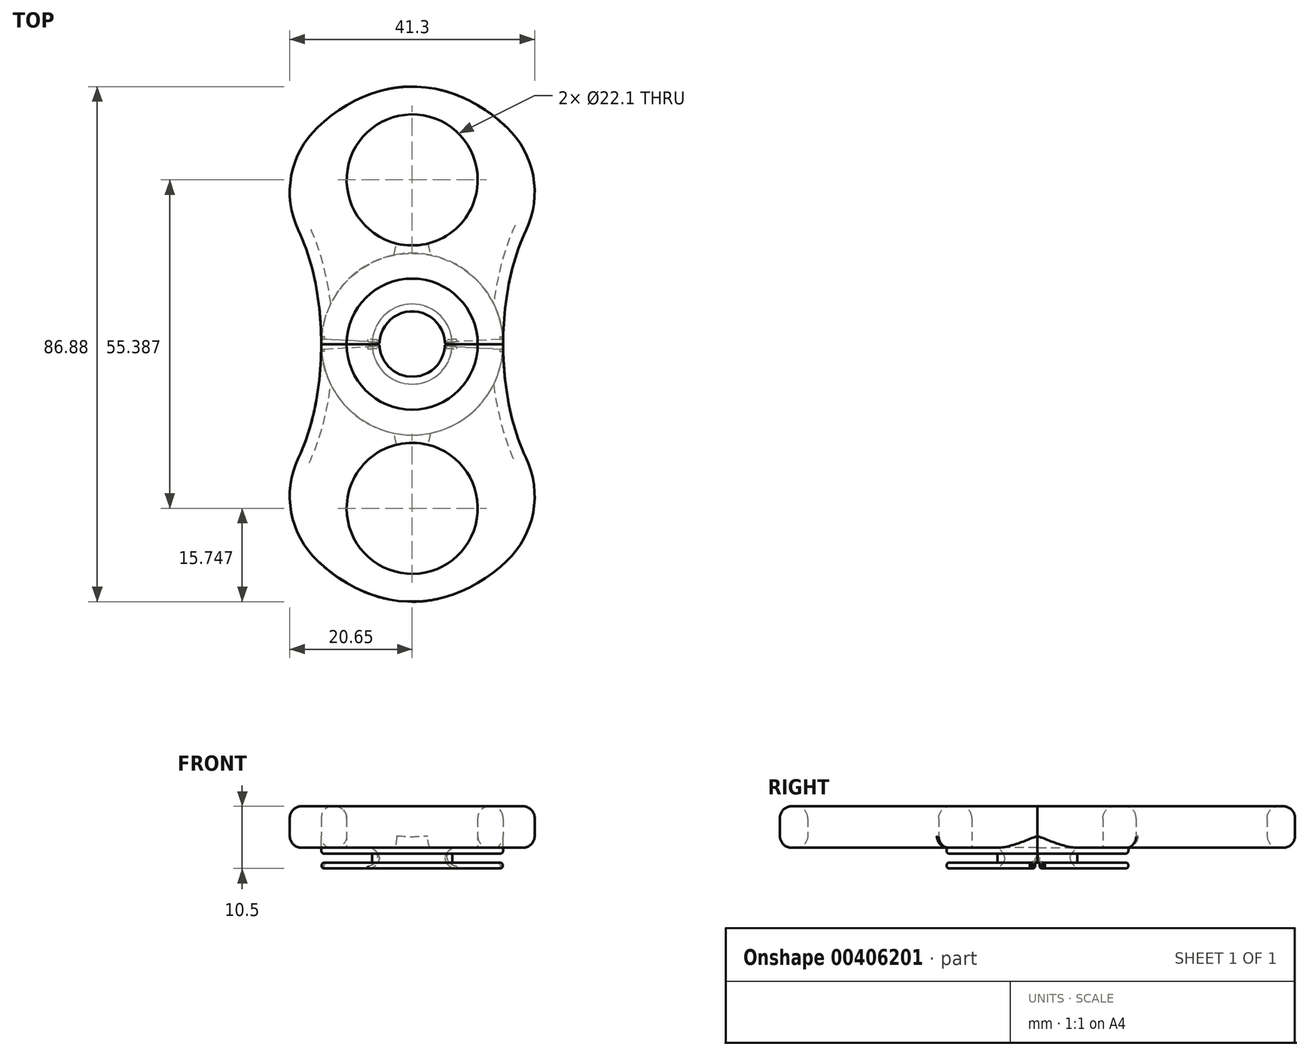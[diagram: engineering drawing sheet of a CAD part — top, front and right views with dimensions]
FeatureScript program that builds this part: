
annotation { "Feature Type Name" : "Feature", "Feature Type Description" : "" }
export const myFeature = defineFeature(function(context is Context, id is Id, definition is map)
    precondition{}
    {
        {
            var Q0;
            Q0=qCreatedBy(makeId("Top.planeOp"),FACE);
            var sketch = newSketch(context, id + "F0", { "sketchPlane" : qUnion([Q0])});
            skCircle(sketch, "E0", {"center": v(0, 0) * mm, "radius": 11.05 * mm});
            skEllipse(sketch, "E1", {"center": v(0, 0) * mm, "majorRadius": 43.44 * mm, "minorRadius": 29.52 * mm, "majorAxis": v(0, 1)});
            skEllipse(sketch, "E2", {"center": v(29.52, 0) * mm, "majorRadius": 28 * mm, "minorRadius": 14.19 * mm, "majorAxis": v(0, -1)});
            skLineSegment(sketch, "E3", {"start": v(0, 58.33) * mm, "end": v(0, -59.11) * mm});
            skEllipse(sketch, "E4", {"center": v(-29.52, 0) * mm, "majorRadius": 27.94 * mm, "minorRadius": 14.94 * mm, "majorAxis": v(0, 1)});
            skCircle(sketch, "E5", {"center": v(0, 27.7) * mm, "radius": 11.05 * mm});
            skLineSegment(sketch, "E6", {"start": v(54.05, 0) * mm, "end": v(-64.12, 0) * mm});
            skCircle(sketch, "E7", {"center": v(0, 0) * mm, "radius": 5.5 * mm});
            skCircle(sketch, "E8", {"center": v(0, 0) * mm, "radius": 15.34 * mm});
            skCircle(sketch, "E9", {"center": v(0, 0) * mm, "radius": 6.75 * mm});
            skSolve(sketch);
        }
        {
            var Q0;
            {var subQ1=sQuery(id+"F0.wireOp",EDGE,"E3");var subQ5=sQuery(id+"F0.wireOp",EDGE,"E0");var subQ6=makeQuery(id+"F0.imprint","INTERSECT",VERTEX,{"disambiguationData":[OD(0.0)],"derivedFrom":[subQ5,subQ1]});Q0=makeQuery(id+"F0.imprint","IMPRINT",FACE,{"disambiguationData":[TD([[makeQuery(id+"F0.imprint","IMPRINT",EDGE,{"disambiguationData":[TD([[subQ6,1.0]])],"derivedFrom":subQ5}),-1.0]])]});}
            var Q1;
            {var subQ1=sQuery(id+"F0.wireOp",EDGE,"E3");var subQ6=sQuery(id+"F0.wireOp",EDGE,"E1");var subQ9=makeQuery(id+"F0.imprint","INTERSECT",VERTEX,{"disambiguationData":[OD(0.0)],"derivedFrom":[subQ6,subQ1]});Q1=makeQuery(id+"F0.imprint","IMPRINT",FACE,{"disambiguationData":[TD([[makeQuery(id+"F0.imprint","IMPRINT",EDGE,{"disambiguationData":[TD([[subQ9,1.0]])],"derivedFrom":subQ6}),1.0]])]});}
            extrude(context, id + "F1", {"entities" : qUnion([Q0, Q1]), "depth" : 7 * mm});
        }
        {
            var Q0;
            {var subQ0=sQuery(id+"F0.wireOp",EDGE,"E3");var subQ1=sQuery(id+"F0.wireOp",EDGE,"E0");var subQ2=makeQuery(id+"F0.imprint","INTERSECT",VERTEX,{"disambiguationData":[OD(0.0)],"derivedFrom":[subQ1,subQ0]});Q0=makeQuery(id+"F0.imprint","IMPRINT",FACE,{"disambiguationData":[TD([[makeQuery(id+"F0.imprint","IMPRINT",EDGE,{"disambiguationData":[TD([[subQ2,1.0]])],"derivedFrom":subQ1}),-1.0]])]});}
            var Q1;
            {var subQ0=sQuery(id+"F0.wireOp",EDGE,"E3");var subQ1=sQuery(id+"F0.wireOp",EDGE,"E0");var subQ2=makeQuery(id+"F0.imprint","INTERSECT",VERTEX,{"disambiguationData":[OD(0.0)],"derivedFrom":[subQ1,subQ0]});Q1=makeQuery(id+"F0.imprint","IMPRINT",FACE,{"disambiguationData":[TD([[makeQuery(id+"F0.imprint","IMPRINT",EDGE,{"disambiguationData":[TD([[subQ2,1.0]])],"derivedFrom":subQ1}),1.0]])]});}
            var Q2;
            {var subQ0=sQuery(id+"F0.wireOp",EDGE,"E9");var subQ1=sQuery(id+"F0.wireOp",EDGE,"E3");var subQ2=makeQuery(id+"F0.imprint","INTERSECT",VERTEX,{"disambiguationData":[OD(0.0)],"derivedFrom":[subQ1,subQ0]});Q2=makeQuery(id+"F0.imprint","IMPRINT",FACE,{"disambiguationData":[TD([[makeQuery(id+"F0.imprint","IMPRINT",EDGE,{"disambiguationData":[TD([[subQ2,-1.0]])],"derivedFrom":subQ1}),1.0]])]});}
            extrude(context, id + "F2", {"entities" : qUnion([Q0, Q1, Q2]), "operationType" : NewBodyOperationType.ADD, "oppositeDirection" : true, "depth" : 1 * mm});
        }
        {
            var Q0;
            {var subQ0=sQuery(id+"F0.wireOp",EDGE,"E9");var subQ1=sQuery(id+"F0.wireOp",EDGE,"E3");var subQ2=makeQuery(id+"F0.imprint","INTERSECT",VERTEX,{"disambiguationData":[OD(0.0)],"derivedFrom":[subQ1,subQ0]});Q0=makeQuery(id+"F0.imprint","IMPRINT",FACE,{"disambiguationData":[TD([[makeQuery(id+"F0.imprint","IMPRINT",EDGE,{"disambiguationData":[TD([[subQ2,-1.0]])],"derivedFrom":subQ1}),1.0]])]});}
            extrude(context, id + "F3", {"entities" : qUnion([Q0]), "operationType" : NewBodyOperationType.ADD, "oppositeDirection" : true, "depth" : 2.5 * mm});
        }
        {
            var Q0;
            {var subQ0=sQuery(id+"F0.wireOp",EDGE,"E9");var subQ1=sQuery(id+"F0.wireOp",EDGE,"E3");var subQ2=makeQuery(id+"F0.imprint","INTERSECT",VERTEX,{"disambiguationData":[OD(0.0)],"derivedFrom":[subQ1,subQ0]});Q0=makeQuery(id+"F0.imprint","IMPRINT",FACE,{"disambiguationData":[TD([[makeQuery(id+"F0.imprint","IMPRINT",EDGE,{"disambiguationData":[TD([[subQ2,-1.0]])],"derivedFrom":subQ1}),1.0]])]});}
            var Q1;
            {var subQ0=sQuery(id+"F0.wireOp",EDGE,"E3");var subQ1=sQuery(id+"F0.wireOp",EDGE,"E0");var subQ2=makeQuery(id+"F0.imprint","INTERSECT",VERTEX,{"disambiguationData":[OD(0.0)],"derivedFrom":[subQ1,subQ0]});Q1=makeQuery(id+"F0.imprint","IMPRINT",FACE,{"disambiguationData":[TD([[makeQuery(id+"F0.imprint","IMPRINT",EDGE,{"disambiguationData":[TD([[subQ2,1.0]])],"derivedFrom":subQ1}),1.0]])]});}
            var Q2;
            {var subQ0=sQuery(id+"F0.wireOp",EDGE,"E3");var subQ1=sQuery(id+"F0.wireOp",EDGE,"E0");var subQ2=makeQuery(id+"F0.imprint","INTERSECT",VERTEX,{"disambiguationData":[OD(0.0)],"derivedFrom":[subQ1,subQ0]});Q2=makeQuery(id+"F0.imprint","IMPRINT",FACE,{"disambiguationData":[TD([[makeQuery(id+"F0.imprint","IMPRINT",EDGE,{"disambiguationData":[TD([[subQ2,1.0]])],"derivedFrom":subQ1}),-1.0]])]});}
            extrude(context, id + "F4", {"entities" : qUnion([Q0, Q1, Q2]), "operationType" : NewBodyOperationType.ADD, "oppositeDirection" : true, "depth" : 3.5 * mm, "hasSecondDirection" : true, "secondDirectionOppositeDirection" : true, "secondDirectionDepth" : 2.5 * mm});
        }
        {
            var Q0;
            Q0=makeQuery(id+"F1.opExtrude","SWEPT_BODY",BODY,{"disambiguationData":[OSD([sQuery(id+"F0.wireOp",EDGE,"E0"),sQuery(id+"F0.wireOp",EDGE,"E1"),sQuery(id+"F0.wireOp",EDGE,"E2"),sQuery(id+"F0.wireOp",EDGE,"E3"),sQuery(id+"F0.wireOp",EDGE,"E5"),sQuery(id+"F0.wireOp",EDGE,"E6")])]});
            var Q1;
            Q1=qCreatedBy(makeId("Right.planeOp"),FACE);
            mirror(context, id + "F5", {"operationType" : NewBodyOperationType.ADD, "entities" : qUnion([Q0]), "mirrorPlane" : qUnion([Q1])});
        }
        {
            var Q0;
            {var subQ0=sQuery(id+"F0.wireOp",EDGE,"E6");var subQ1=sQuery(id+"F0.wireOp",EDGE,"E3");var subQ2=makeQuery(id+"F0.imprint","INTERSECT",VERTEX,{"derivedFrom":[subQ1,subQ0]});Q0=makeQuery(id+"F0.imprint","IMPRINT",FACE,{"disambiguationData":[TD([[makeQuery(id+"F0.imprint","IMPRINT",EDGE,{"disambiguationData":[TD([[subQ2,-1.0]])],"derivedFrom":subQ1}),-1.0]])]});}
            var Q1;
            {var subQ0=sQuery(id+"F0.wireOp",EDGE,"E7");var subQ1=sQuery(id+"F0.wireOp",EDGE,"E3");var subQ2=makeQuery(id+"F0.imprint","INTERSECT",VERTEX,{"disambiguationData":[OD(0.0)],"derivedFrom":[subQ1,subQ0]});Q1=makeQuery(id+"F0.imprint","IMPRINT",FACE,{"disambiguationData":[TD([[makeQuery(id+"F0.imprint","IMPRINT",EDGE,{"disambiguationData":[TD([[subQ2,-1.0]])],"derivedFrom":subQ1}),-1.0]])]});}
            var Q2;
            {var subQ0=sQuery(id+"F0.wireOp",EDGE,"E7");var subQ1=sQuery(id+"F0.wireOp",EDGE,"E3");var subQ2=makeQuery(id+"F0.imprint","INTERSECT",VERTEX,{"disambiguationData":[OD(0.0)],"derivedFrom":[subQ1,subQ0]});Q2=makeQuery(id+"F0.imprint","IMPRINT",FACE,{"disambiguationData":[TD([[makeQuery(id+"F0.imprint","IMPRINT",EDGE,{"disambiguationData":[TD([[subQ2,-1.0]])],"derivedFrom":subQ1}),1.0]])]});}
            var Q3;
            {var subQ0=sQuery(id+"F0.wireOp",EDGE,"E6");var subQ1=sQuery(id+"F0.wireOp",EDGE,"E3");var subQ2=makeQuery(id+"F0.imprint","INTERSECT",VERTEX,{"derivedFrom":[subQ1,subQ0]});Q3=makeQuery(id+"F0.imprint","IMPRINT",FACE,{"disambiguationData":[TD([[makeQuery(id+"F0.imprint","IMPRINT",EDGE,{"disambiguationData":[TD([[subQ2,-1.0]])],"derivedFrom":subQ1}),1.0]])]});}
            extrude(context, id + "F6", {"entities" : qUnion([Q0, Q1, Q2, Q3]), "depth" : 22.66 * mm, "hasSecondDirection" : true, "secondDirectionOppositeDirection" : false, "secondDirectionDepth" : 15.2 * mm});
        }
        {
            var Q0;
            {var subQ0=makeQuery(id+"F4.opExtrude","CAP_FACE",FACE,{"disambiguationData":[OSD([sQuery(id+"F0.wireOp",EDGE,"E3"),sQuery(id+"F0.wireOp",EDGE,"E6"),sQuery(id+"F0.wireOp",EDGE,"E7"),sQuery(id+"F0.wireOp",EDGE,"E8")])],"isStart":false});Q0=makeQuery(id+"F5.boolean.opBoolean","MERGE",FACE,{"derivedFrom":[subQ0,makeQuery(id+"F5.opPattern","COPY",FACE,{"derivedFrom":subQ0,"instanceName":"1"})]});}
            var sketch = newSketch(context, id + "F7", { "sketchPlane" : qUnion([Q0])});
            skLineSegment(sketch, "E10", {"start": v(0, -18) * mm, "end": v(-1, -18) * mm});
            skLineSegment(sketch, "E11", {"start": v(-1, -18) * mm, "end": v(0, 0) * mm});
            skLineSegment(sketch, "E12", {"start": v(0, 0) * mm, "end": v(1, -18) * mm});
            skLineSegment(sketch, "E13", {"start": v(1, -18) * mm, "end": v(0, -18) * mm});
            skLineSegment(sketch, "E14.1.0", {"start": v(8.13, -16.09) * mm, "end": v(0, 0) * mm});
            skLineSegment(sketch, "E14.1.1", {"start": v(0, 0) * mm, "end": v(9.87, -15.09) * mm});
            skLineSegment(sketch, "E14.1.2", {"start": v(9, -15.59) * mm, "end": v(8.13, -16.09) * mm});
            skLineSegment(sketch, "E14.1.3", {"start": v(9.87, -15.09) * mm, "end": v(9, -15.59) * mm});
            skLineSegment(sketch, "E14.2.0", {"start": v(15.09, -9.87) * mm, "end": v(0, 0) * mm});
            skLineSegment(sketch, "E14.2.1", {"start": v(0, 0) * mm, "end": v(16.09, -8.13) * mm});
            skLineSegment(sketch, "E14.2.2", {"start": v(15.59, -9) * mm, "end": v(15.09, -9.87) * mm});
            skLineSegment(sketch, "E14.2.3", {"start": v(16.09, -8.13) * mm, "end": v(15.59, -9) * mm});
            skLineSegment(sketch, "E14.3.0", {"start": v(18, -1) * mm, "end": v(0, 0) * mm});
            skLineSegment(sketch, "E14.3.1", {"start": v(0, 0) * mm, "end": v(18, 1) * mm});
            skLineSegment(sketch, "E14.3.2", {"start": v(18, 0) * mm, "end": v(18, -1) * mm});
            skLineSegment(sketch, "E14.3.3", {"start": v(18, 1) * mm, "end": v(18, 0) * mm});
            skLineSegment(sketch, "E14.4.0", {"start": v(16.09, 8.13) * mm, "end": v(0, 0) * mm});
            skLineSegment(sketch, "E14.4.1", {"start": v(0, 0) * mm, "end": v(15.09, 9.87) * mm});
            skLineSegment(sketch, "E14.4.2", {"start": v(15.59, 9) * mm, "end": v(16.09, 8.13) * mm});
            skLineSegment(sketch, "E14.4.3", {"start": v(15.09, 9.87) * mm, "end": v(15.59, 9) * mm});
            skLineSegment(sketch, "E14.5.0", {"start": v(9.87, 15.09) * mm, "end": v(0, 0) * mm});
            skLineSegment(sketch, "E14.5.1", {"start": v(0, 0) * mm, "end": v(8.13, 16.09) * mm});
            skLineSegment(sketch, "E14.5.2", {"start": v(9, 15.59) * mm, "end": v(9.87, 15.09) * mm});
            skLineSegment(sketch, "E14.5.3", {"start": v(8.13, 16.09) * mm, "end": v(9, 15.59) * mm});
            skLineSegment(sketch, "E14.6.0", {"start": v(1, 18) * mm, "end": v(0, 0) * mm});
            skLineSegment(sketch, "E14.6.1", {"start": v(0, 0) * mm, "end": v(-1, 18) * mm});
            skLineSegment(sketch, "E14.6.2", {"start": v(0, 18) * mm, "end": v(1, 18) * mm});
            skLineSegment(sketch, "E14.6.3", {"start": v(-1, 18) * mm, "end": v(0, 18) * mm});
            skLineSegment(sketch, "E14.7.0", {"start": v(-8.13, 16.09) * mm, "end": v(0, 0) * mm});
            skLineSegment(sketch, "E14.7.1", {"start": v(0, 0) * mm, "end": v(-9.87, 15.09) * mm});
            skLineSegment(sketch, "E14.7.2", {"start": v(-9, 15.59) * mm, "end": v(-8.13, 16.09) * mm});
            skLineSegment(sketch, "E14.7.3", {"start": v(-9.87, 15.09) * mm, "end": v(-9, 15.59) * mm});
            skLineSegment(sketch, "E14.8.0", {"start": v(-15.09, 9.87) * mm, "end": v(0, 0) * mm});
            skLineSegment(sketch, "E14.8.1", {"start": v(0, 0) * mm, "end": v(-16.09, 8.13) * mm});
            skLineSegment(sketch, "E14.8.2", {"start": v(-15.59, 9) * mm, "end": v(-15.09, 9.87) * mm});
            skLineSegment(sketch, "E14.8.3", {"start": v(-16.09, 8.13) * mm, "end": v(-15.59, 9) * mm});
            skLineSegment(sketch, "E14.9.0", {"start": v(-18, 1) * mm, "end": v(0, 0) * mm});
            skLineSegment(sketch, "E14.9.1", {"start": v(0, 0) * mm, "end": v(-18, -1) * mm});
            skLineSegment(sketch, "E14.9.2", {"start": v(-18, 0) * mm, "end": v(-18, 1) * mm});
            skLineSegment(sketch, "E14.9.3", {"start": v(-18, -1) * mm, "end": v(-18, 0) * mm});
            skLineSegment(sketch, "E14.10.0", {"start": v(-16.09, -8.13) * mm, "end": v(0, 0) * mm});
            skLineSegment(sketch, "E14.10.1", {"start": v(0, 0) * mm, "end": v(-15.09, -9.87) * mm});
            skLineSegment(sketch, "E14.10.2", {"start": v(-15.59, -9) * mm, "end": v(-16.09, -8.13) * mm});
            skLineSegment(sketch, "E14.10.3", {"start": v(-15.09, -9.87) * mm, "end": v(-15.59, -9) * mm});
            skLineSegment(sketch, "E14.11.0", {"start": v(-9.87, -15.09) * mm, "end": v(0, 0) * mm});
            skLineSegment(sketch, "E14.11.1", {"start": v(0, 0) * mm, "end": v(-8.13, -16.09) * mm});
            skLineSegment(sketch, "E14.11.2", {"start": v(-9, -15.59) * mm, "end": v(-9.87, -15.09) * mm});
            skLineSegment(sketch, "E14.11.3", {"start": v(-8.13, -16.09) * mm, "end": v(-9, -15.59) * mm});
            skPoint(sketch, "E14.center", {"position": v(0, 0) * mm});
            skSolve(sketch);
        }
        {
            var Q0;
            {var subQ0=makeQuery(id+"F1.opExtrude","CAP_EDGE",EDGE,{"disambiguationData":[OSD([sQuery(id+"F0.wireOp",EDGE,"E5")])],"isStart":true});Q0=makeQuery(id+"F5.boolean.opBoolean","MERGE",EDGE,{"derivedFrom":[subQ0,makeQuery(id+"F5.opPattern","COPY",EDGE,{"derivedFrom":subQ0,"instanceName":"1"})]});}
            var Q1;
            Q1=makeQuery(id+"F1.opExtrude","CAP_EDGE",EDGE,{"disambiguationData":[OSD([sQuery(id+"F0.wireOp",EDGE,"E2")])],"isStart":true});
            var Q2;
            Q2=makeQuery(id+"F1.opExtrude","CAP_EDGE",EDGE,{"disambiguationData":[OSD([sQuery(id+"F0.wireOp",EDGE,"E2")])],"isStart":false});
            var Q3;
            Q3=makeQuery(id+"F5.opPattern","COPY",EDGE,{"derivedFrom":makeQuery(id+"F1.opExtrude","CAP_EDGE",EDGE,{"disambiguationData":[OSD([sQuery(id+"F0.wireOp",EDGE,"E2")])],"isStart":true}),"instanceName":"1"});
            var Q4;
            {var subQ0=makeQuery(id+"F1.opExtrude","CAP_EDGE",EDGE,{"disambiguationData":[OSD([sQuery(id+"F0.wireOp",EDGE,"E1")])],"isStart":true});Q4=makeQuery(id+"F5.boolean.opBoolean","MERGE",EDGE,{"derivedFrom":[subQ0,makeQuery(id+"F5.opPattern","COPY",EDGE,{"derivedFrom":subQ0,"instanceName":"1"})]});}
            var Q5;
            {var subQ0=makeQuery(id+"F4.opExtrude","CAP_EDGE",EDGE,{"disambiguationData":[OSD([sQuery(id+"F0.wireOp",EDGE,"E7")])],"isStart":false});Q5=makeQuery(id+"F5.boolean.opBoolean","MERGE",EDGE,{"derivedFrom":[subQ0,makeQuery(id+"F5.opPattern","COPY",EDGE,{"derivedFrom":subQ0,"instanceName":"1"})]});}
            var Q6;
            {var subQ0=makeQuery(id+"F2.opExtrude","CAP_EDGE",EDGE,{"disambiguationData":[OSD([sQuery(id+"F0.wireOp",EDGE,"E7")])],"isStart":true});Q6=makeQuery(id+"F5.boolean.opBoolean","MERGE",EDGE,{"derivedFrom":[subQ0,makeQuery(id+"F5.opPattern","COPY",EDGE,{"derivedFrom":subQ0,"instanceName":"1"})]});}
            var Q7;
            {var subQ0=makeQuery(id+"F1.opExtrude","CAP_EDGE",EDGE,{"disambiguationData":[OSD([sQuery(id+"F0.wireOp",EDGE,"E1")])],"isStart":false});Q7=makeQuery(id+"F5.boolean.opBoolean","MERGE",EDGE,{"derivedFrom":[subQ0,makeQuery(id+"F5.opPattern","COPY",EDGE,{"derivedFrom":subQ0,"instanceName":"1"})]});}
            var Q8;
            {var subQ0=makeQuery(id+"F1.opExtrude","CAP_EDGE",EDGE,{"disambiguationData":[OSD([sQuery(id+"F0.wireOp",EDGE,"E5")])],"isStart":false});Q8=makeQuery(id+"F5.boolean.opBoolean","MERGE",EDGE,{"derivedFrom":[subQ0,makeQuery(id+"F5.opPattern","COPY",EDGE,{"derivedFrom":subQ0,"instanceName":"1"})]});}
            var Q9;
            {var subQ0=makeQuery(id+"F1.opExtrude","CAP_EDGE",EDGE,{"disambiguationData":[OSD([sQuery(id+"F0.wireOp",EDGE,"E0")])],"isStart":false});Q9=makeQuery(id+"F5.boolean.opBoolean","MERGE",EDGE,{"derivedFrom":[subQ0,makeQuery(id+"F5.opPattern","COPY",EDGE,{"derivedFrom":subQ0,"instanceName":"1"})]});}
            var Q10;
            Q10=makeQuery(id+"F5.opPattern","COPY",EDGE,{"derivedFrom":makeQuery(id+"F1.opExtrude","CAP_EDGE",EDGE,{"disambiguationData":[OSD([sQuery(id+"F0.wireOp",EDGE,"E2")])],"isStart":false}),"instanceName":"1"});
            fillet(context, id + "F8", {"entities" : qUnion([Q0, Q1, Q2, Q3, Q4, Q5, Q6, Q7, Q8, Q9, Q10]), "radius" : 2 * mm, "tangentPropagation" : true, "allowEdgeOverflow" : false});
        }
        {
            var Q0;
            Q0=makeQuery(id+"F5.opPattern","COPY",EDGE,{"derivedFrom":makeQuery(id+"F1.opExtrude","SWEPT_EDGE",EDGE,{"disambiguationData":[OSD([sQuery(id+"F0.wireOp",EDGE,"E1"),sQuery(id+"F0.wireOp",EDGE,"E2")])]}),"instanceName":"1"});
            var Q1;
            Q1=makeQuery(id+"F1.opExtrude","SWEPT_EDGE",EDGE,{"disambiguationData":[OSD([sQuery(id+"F0.wireOp",EDGE,"E1"),sQuery(id+"F0.wireOp",EDGE,"E2")])]});
            fillet(context, id + "F9", {"entities" : qUnion([Q0, Q1]), "radius" : 15 * mm, "tangentPropagation" : true, "allowEdgeOverflow" : false});
        }
        {
            var Q0;
            {var subQ0=makeQuery(id+"F4.opExtrude","CAP_EDGE",EDGE,{"disambiguationData":[OSD([sQuery(id+"F0.wireOp",EDGE,"E8")])],"isStart":false});Q0=makeQuery(id+"F5.boolean.opBoolean","MERGE",EDGE,{"derivedFrom":[subQ0,makeQuery(id+"F5.opPattern","COPY",EDGE,{"derivedFrom":subQ0,"instanceName":"1"})]});}
            var Q1;
            {var subQ0=makeQuery(id+"F2.opExtrude","CAP_EDGE",EDGE,{"disambiguationData":[OSD([sQuery(id+"F0.wireOp",EDGE,"E8")])],"isStart":false});Q1=makeQuery(id+"F5.boolean.opBoolean","MERGE",EDGE,{"derivedFrom":[subQ0,makeQuery(id+"F5.opPattern","COPY",EDGE,{"derivedFrom":subQ0,"instanceName":"1"})]});}
            var Q2;
            {var subQ0=makeQuery(id+"F4.opExtrude","CAP_EDGE",EDGE,{"disambiguationData":[OSD([sQuery(id+"F0.wireOp",EDGE,"E8")])],"isStart":true});Q2=makeQuery(id+"F5.boolean.opBoolean","MERGE",EDGE,{"derivedFrom":[subQ0,makeQuery(id+"F5.opPattern","COPY",EDGE,{"derivedFrom":subQ0,"instanceName":"1"})]});}
            var Q3;
            {var subQ0=makeQuery(id+"F2.opExtrude","CAP_EDGE",EDGE,{"disambiguationData":[OSD([sQuery(id+"F0.wireOp",EDGE,"E8")])],"isStart":true});Q3=makeQuery(id+"F5.boolean.opBoolean","MERGE",EDGE,{"derivedFrom":[subQ0,makeQuery(id+"F5.opPattern","COPY",EDGE,{"derivedFrom":subQ0,"instanceName":"1"})]});}
            var Q4;
            {var subQ0=makeQuery(id+"F2.opExtrude","CAP_EDGE",EDGE,{"disambiguationData":[OSD([sQuery(id+"F0.wireOp",EDGE,"E8")])],"isStart":true});Q4=makeQuery(id+"F5.boolean.opBoolean","MERGE",EDGE,{"derivedFrom":[subQ0,makeQuery(id+"F5.opPattern","COPY",EDGE,{"derivedFrom":subQ0,"instanceName":"1"})]});}
            fillet(context, id + "F10", {"entities" : qUnion([Q0, Q1, Q2, Q3, Q4]), "radius" : 0.5 * mm, "tangentPropagation" : true, "allowEdgeOverflow" : false});
        }
        {
            var Q0;
            Q0=makeQuery(id+"F1.opExtrude","SWEPT_BODY",BODY,{"disambiguationData":[OSD([sQuery(id+"F0.wireOp",EDGE,"E0"),sQuery(id+"F0.wireOp",EDGE,"E1"),sQuery(id+"F0.wireOp",EDGE,"E2"),sQuery(id+"F0.wireOp",EDGE,"E3"),sQuery(id+"F0.wireOp",EDGE,"E5"),sQuery(id+"F0.wireOp",EDGE,"E6")])]});
            var Q1;
            Q1=makeQuery(id+"F6.opExtrude","CAP_EDGE",EDGE,{"disambiguationData":[OSD([sQuery(id+"F0.wireOp",EDGE,"E7")])],"isStart":true});
            circularPattern(context, id + "F11", {"operationType" : NewBodyOperationType.ADD, "entities" : qUnion([Q0]), "axis" : qUnion([Q1]), "angle" : 360 * degree, "instanceCount" : 2, "equalSpace" : true});
        }
        {
            var Q0;
            {var subQ9=sQuery(id+"F7.wireOp",EDGE,"E14.9.0");Q0=makeQuery(id+"F7.imprint","IMPRINT",FACE,{"disambiguationData":[TD([[makeQuery(id+"F7.imprint","IMPRINT",EDGE,{"derivedFrom":subQ9}),-1.0]])]});}
            var Q1;
            {var subQ7=makeQuery(id+"F5.opPattern","COPY",EDGE,{"derivedFrom":makeQuery(id+"F4.opExtrude","CAP_EDGE",EDGE,{"disambiguationData":[OSD([sQuery(id+"F0.wireOp",EDGE,"E6")])],"isStart":false}),"instanceName":"1"});Q1=makeQuery(id+"F7.imprint","IMPRINT",FACE,{"disambiguationData":[TD([[makeQuery(id+"F7.imprint","IMPRINT",EDGE,{"derivedFrom":subQ7}),-1.0]])]});}
            var Q2;
            {var subQ7=makeQuery(id+"F4.opExtrude","CAP_EDGE",EDGE,{"disambiguationData":[OSD([sQuery(id+"F0.wireOp",EDGE,"E6")])],"isStart":false});Q2=makeQuery(id+"F7.imprint","IMPRINT",FACE,{"disambiguationData":[TD([[makeQuery(id+"F7.imprint","IMPRINT",EDGE,{"derivedFrom":subQ7}),1.0]])]});}
            var Q3;
            {var subQ2=sQuery(id+"F7.wireOp",EDGE,"E14.3.1");Q3=makeQuery(id+"F7.imprint","IMPRINT",FACE,{"disambiguationData":[TD([[makeQuery(id+"F7.imprint","IMPRINT",EDGE,{"derivedFrom":subQ2}),-1.0]])]});}
            extrude(context, id + "F12", {"entities" : qUnion([Q0, Q1, Q2, Q3]), "operationType" : NewBodyOperationType.REMOVE, "oppositeDirection" : true, "depth" : 1 * mm});
        }
        {
            var Q0;
            {var subQ0=sQuery(id+"F0.wireOp",EDGE,"E8");var subQ3=sQuery(id+"F0.wireOp",EDGE,"E7");var subQ6=makeQuery(id+"F4.opExtrude","CAP_FACE",FACE,{"disambiguationData":[OSD([sQuery(id+"F0.wireOp",EDGE,"E3"),sQuery(id+"F0.wireOp",EDGE,"E6"),subQ3,subQ0])],"isStart":false});var subQ7=makeQuery(id+"F5.boolean.opBoolean","MERGE",FACE,{"derivedFrom":[subQ6,makeQuery(id+"F5.opPattern","COPY",FACE,{"derivedFrom":subQ6,"instanceName":"1"})]});Q0=makeQuery(id+"FEYc9VW4fI0q4IH_2.1.F12.boolean.opBoolean","SPLIT",FACE,{"disambiguationData":[TD([makeQuery(id+"F12.boolean.opBoolean","COPY",FACE,{"derivedFrom":makeQuery(id+"F12.opExtrude","SWEPT_FACE",FACE,{"disambiguationData":[OSD([sQuery(id+"F7.wireOp",EDGE,"E14.9.0")])]})})])],"derivedFrom":makeQuery(id+"F11.boolean.opBoolean","MERGE",FACE,{"derivedFrom":[subQ7,makeQuery(id+"F11.opPattern","COPY",FACE,{"derivedFrom":subQ7,"instanceName":"1"})]})});}
            var Q1;
            {var subQ0=sQuery(id+"F0.wireOp",EDGE,"E8");var subQ3=sQuery(id+"F0.wireOp",EDGE,"E7");var subQ6=makeQuery(id+"F4.opExtrude","CAP_FACE",FACE,{"disambiguationData":[OSD([sQuery(id+"F0.wireOp",EDGE,"E3"),sQuery(id+"F0.wireOp",EDGE,"E6"),subQ3,subQ0])],"isStart":false});var subQ7=makeQuery(id+"F5.boolean.opBoolean","MERGE",FACE,{"derivedFrom":[subQ6,makeQuery(id+"F5.opPattern","COPY",FACE,{"derivedFrom":subQ6,"instanceName":"1"})]});Q1=makeQuery(id+"FEYc9VW4fI0q4IH_2.1.F12.boolean.opBoolean","SPLIT",FACE,{"disambiguationData":[TD([makeQuery(id+"F12.boolean.opBoolean","COPY",FACE,{"derivedFrom":makeQuery(id+"F12.opExtrude","SWEPT_FACE",FACE,{"disambiguationData":[OSD([sQuery(id+"F7.wireOp",EDGE,"E14.9.1")])]})})])],"derivedFrom":makeQuery(id+"F11.boolean.opBoolean","MERGE",FACE,{"derivedFrom":[subQ7,makeQuery(id+"F11.opPattern","COPY",FACE,{"derivedFrom":subQ7,"instanceName":"1"})]})});}
            var Q2;
            {var subQ0=sQuery(id+"F0.wireOp",EDGE,"E7");var subQ1=makeQuery(id+"F4.opExtrude","CAP_EDGE",EDGE,{"disambiguationData":[OSD([subQ0])],"isStart":false});var subQ2=makeQuery(id+"F8.opFillet","BLEND_FACE",FACE,{"disambiguationData":[OSD([subQ0]),TDD([makeQuery(id+"F5.boolean.opBoolean","MERGE",EDGE,{"derivedFrom":[subQ1,makeQuery(id+"F5.opPattern","COPY",EDGE,{"derivedFrom":subQ1,"instanceName":"1"})]})])]});Q2=makeQuery(id+"F11.boolean.opBoolean","MERGE",FACE,{"derivedFrom":[subQ2,makeQuery(id+"F11.opPattern","COPY",FACE,{"derivedFrom":subQ2,"instanceName":"1"})]});}
            fillet(context, id + "F13", {"entities" : qUnion([Q0, Q1, Q2]), "radius" : 0.4 * mm, "tangentPropagation" : true, "allowEdgeOverflow" : false});
        }
        {
            var Q0;
            Q0=makeQuery(id+"F6.opExtrude","SWEPT_BODY",BODY,{"disambiguationData":[OSD([sQuery(id+"F0.wireOp",EDGE,"E7")])]});
            deleteBodies(context, id + "F14", {"entities" : qUnion([Q0])});
        }
    });
